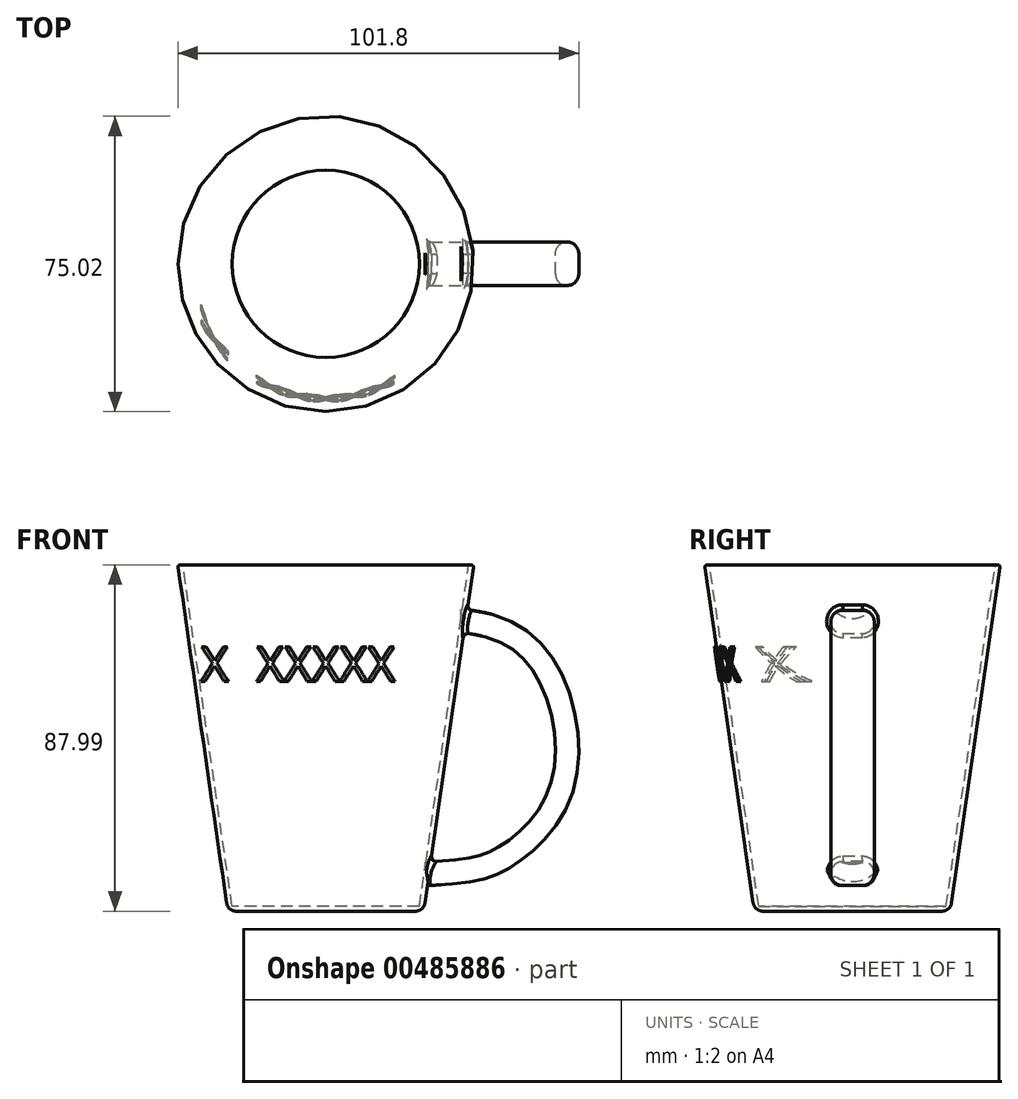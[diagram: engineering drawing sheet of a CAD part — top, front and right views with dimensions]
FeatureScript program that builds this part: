
annotation { "Feature Type Name" : "Feature", "Feature Type Description" : "" }
export const myFeature = defineFeature(function(context is Context, id is Id, definition is map)
    precondition{}
    {
        {
            var Q0;
            Q0=qCreatedBy(makeId("Front.planeOp"),FACE);
            var sketch = newSketch(context, id + "F0", { "sketchPlane" : qUnion([Q0])});
            skLineSegment(sketch, "E0", {"start": v(0, 0) * mm, "end": v(25.4, 0) * mm});
            skLineSegment(sketch, "E1", {"start": v(25.4, 0) * mm, "end": v(38.1, 87.99) * mm});
            skLineSegment(sketch, "E2", {"start": v(38.1, 87.99) * mm, "end": v(0, 87.99) * mm});
            skLineSegment(sketch, "E3", {"start": v(0, 87.99) * mm, "end": v(0, 0) * mm});
            skSolve(sketch);
        }
        {
            var Q0;
            Q0=makeQuery(id+"F0.imprint","IMPRINT",FACE,{"disambiguationData":[TD([[makeQuery(id+"F0.imprint","IMPRINT",EDGE,{"derivedFrom":sQuery(id+"F0.wireOp",EDGE,"E0")}),1.0]])]});
            var Q1;
            Q1=sQuery(id+"F0.wireOp",EDGE,"E3");
            revolve(context, id + "F1", {"entities" : qUnion([Q0]), "axis" : qUnion([Q1]), "revolveType" : RevolveType.FULL});
        }
        {
            var Q0;
            Q0=makeQuery(id+"F1.opRevolve","SWEPT_FACE",FACE,{"disambiguationData":[OSD([sQuery(id+"F0.wireOp",EDGE,"E2")])]});
            shell(context, id + "F2", {"entities" : qUnion([Q0]), "thickness" : 2.54 * mm});
        }
        {
            var Q0;
            Q0=makeQuery(id+"F1.opRevolve","SWEPT_EDGE",EDGE,{"disambiguationData":[OSD([sQuery(id+"F0.wireOp",EDGE,"E1"),sQuery(id+"F0.wireOp",EDGE,"E2")])]});
            var Q1;
            Q1=makeQuery(id+"FDXy1sfSSZcNKEJ_1.opShell","OFFSET_EDGE",EDGE,{"disambiguationData":[OSD([sQuery(id+"F0.wireOp",EDGE,"E1"),sQuery(id+"F0.wireOp",EDGE,"E2")])]});
            fillet(context, id + "F3", {"entities" : qUnion([Q0, Q1]), "radius" : 0.22 * mm, "tangentPropagation" : true, "allowEdgeOverflow" : false});
        }
        {
            var Q0;
            Q0=qCreatedBy(makeId("Front.planeOp"),FACE);
            var sketch = newSketch(context, id + "F4", { "sketchPlane" : qUnion([Q0])});
            skText(sketch, "E4", { "text": "XXXXXXXXX\n", "fontName": "OpenSans-Regular.ttf"});
            const initialGuessF4  = {"E4": [-0.03175, 0.05845, 1, 0, 0.0088]};
            skSetInitialGuess(sketch, initialGuessF4);
            skSolve(sketch);
        }
        {
            var Q0;
            Q0=makeQuery(id+"F4.imprint","IMPRINT",FACE,{"disambiguationData":[TD([[makeQuery(id+"F4.imprint","IMPRINT",EDGE,{"derivedFrom":sQuery(id+"F4.wireOp",EDGE,"E4.sketch_text.stroke-0")}),-1.0]])]});
            var Q1;
            Q1=makeQuery(id+"F4.imprint","IMPRINT",FACE,{"disambiguationData":[TD([[makeQuery(id+"F4.imprint","IMPRINT",EDGE,{"derivedFrom":sQuery(id+"F4.wireOp",EDGE,"E4.sketch_text.stroke-25")}),-1.0]])]});
            var Q2;
            Q2=makeQuery(id+"F4.imprint","IMPRINT",FACE,{"disambiguationData":[TD([[makeQuery(id+"F4.imprint","IMPRINT",EDGE,{"derivedFrom":sQuery(id+"F4.wireOp",EDGE,"E4.sketch_text.stroke-38")}),-1.0]])]});
            var Q3;
            Q3=makeQuery(id+"F4.imprint","IMPRINT",FACE,{"disambiguationData":[TD([[makeQuery(id+"F4.imprint","IMPRINT",EDGE,{"derivedFrom":sQuery(id+"F4.wireOp",EDGE,"E4.sketch_text.stroke-56")}),-1.0]])]});
            var Q4;
            Q4=makeQuery(id+"F4.imprint","IMPRINT",FACE,{"disambiguationData":[TD([[makeQuery(id+"F4.imprint","IMPRINT",EDGE,{"derivedFrom":sQuery(id+"F4.wireOp",EDGE,"E4.sketch_text.stroke-70")}),-1.0]])]});
            var Q5;
            Q5=makeQuery(id+"F4.imprint","IMPRINT",FACE,{"disambiguationData":[TD([[makeQuery(id+"F4.imprint","IMPRINT",EDGE,{"derivedFrom":sQuery(id+"F4.wireOp",EDGE,"E4.sketch_text.stroke-82")}),-1.0]])]});
            extrude(context, id + "F5", {"entities" : qUnion([Q0, Q1, Q2, Q3, Q4, Q5]), "operationType" : NewBodyOperationType.INTERSECT, "depth" : 47.27 * mm});
        }
        {
            var Q0;
            Q0=qCreatedBy(makeId("Front.planeOp"),FACE);
            var sketch = newSketch(context, id + "F6", { "sketchPlane" : qUnion([Q0])});
            skLineSegment(sketch, "E5", {"start": v(0, 0) * mm, "end": v(24.9, 0) * mm});
            skLineSegment(sketch, "E6", {"start": v(24.9, 0) * mm, "end": v(37.6, 87.99) * mm});
            skLineSegment(sketch, "E7", {"start": v(37.6, 87.99) * mm, "end": v(0, 87.99) * mm});
            skLineSegment(sketch, "E8", {"start": v(0, 87.99) * mm, "end": v(0, 0) * mm});
            skSolve(sketch);
        }
        {
            var Q0;
            Q0=makeQuery(id+"F6.imprint","IMPRINT",FACE,{"disambiguationData":[TD([[makeQuery(id+"F6.imprint","IMPRINT",EDGE,{"derivedFrom":sQuery(id+"F6.wireOp",EDGE,"E5")}),1.0]])]});
            var Q1;
            Q1=sQuery(id+"F6.wireOp",EDGE,"E8");
            revolve(context, id + "F7", {"operationType" : NewBodyOperationType.ADD, "entities" : qUnion([Q0]), "axis" : qUnion([Q1]), "revolveType" : RevolveType.FULL});
        }
        {
            var Q0;
            Q0=makeQuery(id+"F7.opRevolve","SWEPT_FACE",FACE,{"disambiguationData":[OSD([sQuery(id+"F6.wireOp",EDGE,"E7")])]});
            shell(context, id + "F8", {"entities" : qUnion([Q0]), "thickness" : 1.27 * mm});
        }
        {
            var Q0;
            Q0=makeQuery(id+"F7.opRevolve","SWEPT_EDGE",EDGE,{"disambiguationData":[OSD([sQuery(id+"F6.wireOp",EDGE,"E5"),sQuery(id+"F6.wireOp",EDGE,"E6")])]});
            fillet(context, id + "F9", {"entities" : qUnion([Q0]), "radius" : 2.54 * mm, "tangentPropagation" : true, "allowEdgeOverflow" : false});
        }
        {
            var Q0;
            Q0=makeQuery(id+"F7.opRevolve","SWEPT_EDGE",EDGE,{"disambiguationData":[OSD([sQuery(id+"F6.wireOp",EDGE,"E6"),sQuery(id+"F6.wireOp",EDGE,"E7")])]});
            var Q1;
            Q1=makeQuery(id+"F8.opShell","OFFSET_EDGE",EDGE,{"disambiguationData":[OSD([sQuery(id+"F6.wireOp",EDGE,"E6"),sQuery(id+"F6.wireOp",EDGE,"E7")])]});
            fillet(context, id + "F10", {"entities" : qUnion([Q0, Q1]), "radius" : 0.5 * mm, "tangentPropagation" : true, "allowEdgeOverflow" : false});
        }
        {
            var Q0;
            Q0=qCreatedBy(makeId("Right.planeOp"),FACE);
            cPlane(context, id + "F11", {"entities" : qUnion([Q0]), "cplaneType" : CPlaneType.OFFSET, "offset" : 35.05 * mm, "width" : 152.4 * mm, "height" : 152.4 * mm});
        }
        {
            var Q0;
            Q0=qCreatedBy(id+"F11.planeOp",FACE);
            var sketch = newSketch(context, id + "F12", { "sketchPlane" : qUnion([Q0])});
            skLineSegment(sketch, "E9", {"start": v(-2.52, 76.65) * mm, "end": v(2.56, 76.65) * mm});
            skArc(sketch, "E10", {"start": v(-2.52, 76.65) * mm, "mid": v(-5.5, 73.67) * mm, "end": v(-2.52, 70.68) * mm});
            skLineSegment(sketch, "E11", {"start": v(-2.52, 70.68) * mm, "end": v(2.56, 70.68) * mm});
            skArc(sketch, "E12", {"start": v(2.56, 70.68) * mm, "mid": v(5.55, 73.67) * mm, "end": v(2.56, 76.65) * mm});
            skSolve(sketch);
        }
        {
            var Q0;
            Q0=qCreatedBy(makeId("Front.planeOp"),FACE);
            var sketch = newSketch(context, id + "F13", { "sketchPlane" : qUnion([Q0])});
            skFitSpline(sketch, "E13", {"points": [v(34.36, 73.77) * mm, v(56.62, 60.34) * mm, v(59.68, 30.37) * mm, v(45.62, 13.81) * mm, v(25.68, 9.43) * mm], "startDerivative": vector(128.67, -8.21) * mm, "endDerivative": vector(-147.47, -8.8) * mm});
            skSolve(sketch);
        }
        {
            var Q0;
            Q0=makeQuery(id+"F12.imprint","IMPRINT",FACE,{"disambiguationData":[TD([[makeQuery(id+"F12.imprint","IMPRINT",EDGE,{"derivedFrom":sQuery(id+"F12.wireOp",EDGE,"E9")}),-1.0]])]});
            var Q1;
            Q1=sQuery(id+"F13.wireOp",EDGE,"E13");
            sweep(context, id + "F14", {"operationType" : NewBodyOperationType.ADD, "profiles" : qUnion([Q0]), "path" : qUnion([Q1])});
        }
        {
            var Q0;
            Q0=makeQuery(id+"F14.boolean.opBoolean","INTERSECT",EDGE,{"disambiguationData":[OD(1.0)],"derivedFrom":[makeQuery(id+"F7.boolean.opBoolean","SPLIT",FACE,{"disambiguationData":[TD([makeQuery(id+"F5.boolean.opBoolean","COPY",FACE,{"derivedFrom":makeQuery(id+"F5.boolean.toolComplement.opBoolean","COPY",FACE,{"derivedFrom":makeQuery(id+"F5.opExtrude","SWEPT_FACE",FACE,{"disambiguationData":[OSD([sQuery(id+"F4.wireOp",EDGE,"E4.sketch_text.stroke-0")])]})})})])],"derivedFrom":makeQuery(id+"F7.opRevolve","SWEPT_FACE",FACE,{"disambiguationData":[OSD([sQuery(id+"F6.wireOp",EDGE,"E6")])]})}),makeQuery(id+"F14.opSweep","SWEPT_FACE",FACE,{"disambiguationData":[OSD([sQuery(id+"F12.wireOp",EDGE,"E10"),sQuery(id+"F13.wireOp",EDGE,"E13")])]})]});
            var Q1;
            Q1=makeQuery(id+"F14.boolean.opBoolean","INTERSECT",EDGE,{"disambiguationData":[OD(0.0)],"derivedFrom":[makeQuery(id+"F7.boolean.opBoolean","SPLIT",FACE,{"disambiguationData":[TD([makeQuery(id+"F5.boolean.opBoolean","COPY",FACE,{"derivedFrom":makeQuery(id+"F5.boolean.toolComplement.opBoolean","COPY",FACE,{"derivedFrom":makeQuery(id+"F5.opExtrude","SWEPT_FACE",FACE,{"disambiguationData":[OSD([sQuery(id+"F4.wireOp",EDGE,"E4.sketch_text.stroke-0")])]})})})])],"derivedFrom":makeQuery(id+"F7.opRevolve","SWEPT_FACE",FACE,{"disambiguationData":[OSD([sQuery(id+"F6.wireOp",EDGE,"E6")])]})}),makeQuery(id+"F14.opSweep","SWEPT_FACE",FACE,{"disambiguationData":[OSD([sQuery(id+"F12.wireOp",EDGE,"E10"),sQuery(id+"F13.wireOp",EDGE,"E13")])]})]});
            fillet(context, id + "F15", {"entities" : qUnion([Q0, Q1]), "radius" : 1.27 * mm, "tangentPropagation" : true, "allowEdgeOverflow" : false});
        }
    });
